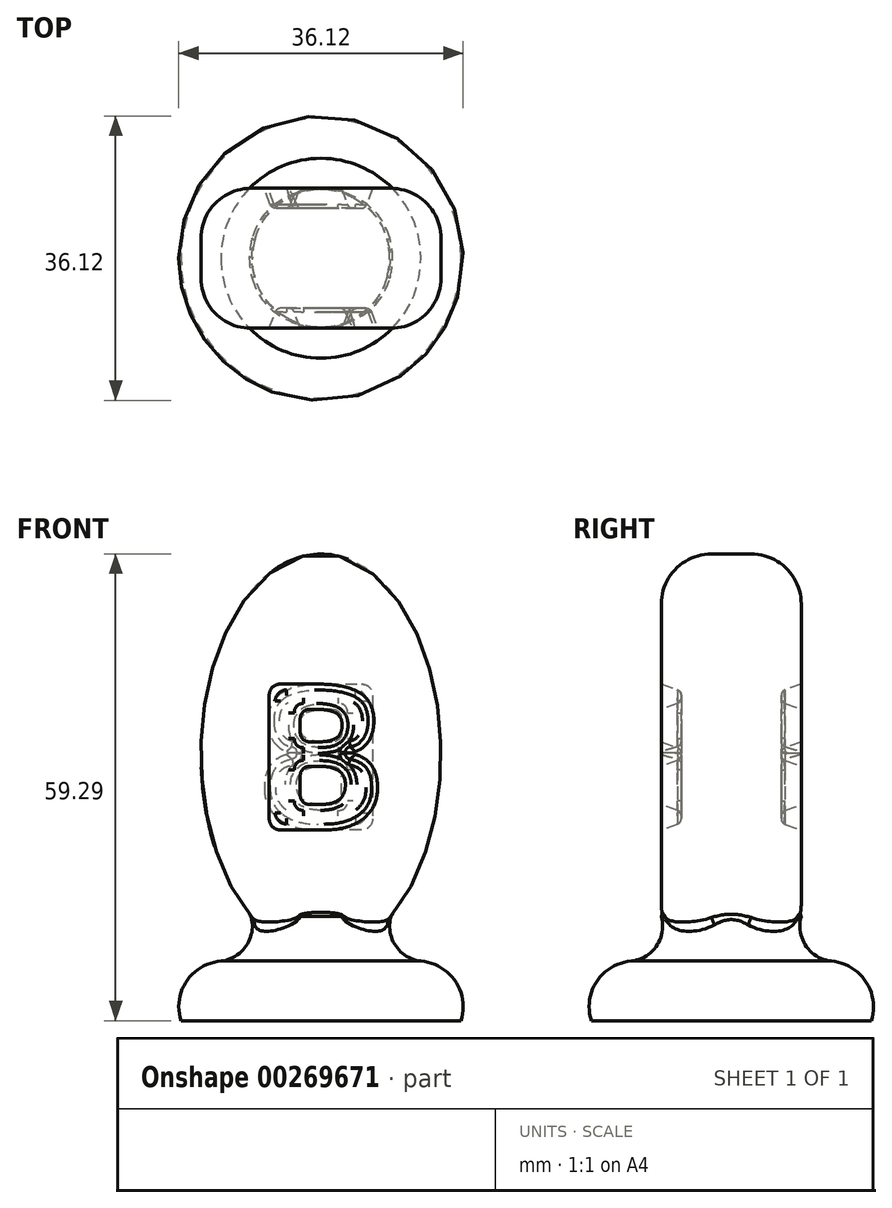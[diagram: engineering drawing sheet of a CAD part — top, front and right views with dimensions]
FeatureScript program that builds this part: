
annotation { "Feature Type Name" : "Feature", "Feature Type Description" : "" }
export const myFeature = defineFeature(function(context is Context, id is Id, definition is map)
    precondition{}
    {
        {
            var Q0;
            Q0=qCreatedBy(makeId("Front.planeOp"),FACE);
            var sketch = newSketch(context, id + "F0", { "sketchPlane" : qUnion([Q0])});
            skEllipse(sketch, "E0", {"center": v(0, 33.89) * mm, "majorRadius": 25.4 * mm, "minorRadius": 15.24 * mm, "majorAxis": v(0, -1)});
            skLineSegment(sketch, "E1", {"start": v(0, 0) * mm, "end": v(0, 8.49) * mm, "construction": true});
            skSolve(sketch);
        }
        {
            var Q0;
            Q0=qSketchRegion(id+"F0",true);
            extrude(context, id + "F1", {"entities" : qUnion([Q0]), "depth" : 8.9 * mm});
        }
        {
            var Q0;
            Q0=makeQuery(id+"F1.opExtrude","CAP_EDGE",EDGE,{"disambiguationData":[OSD([sQuery(id+"F0.wireOp",EDGE,"E0")])],"isStart":false});
            fillet(context, id + "F2", {"entities" : qUnion([Q0]), "radius" : 6.35 * mm, "tangentPropagation" : true, "allowEdgeOverflow" : false});
        }
        {
            var Q0;
            Q0=qCreatedBy(makeId("Front.planeOp"),FACE);
            var sketch = newSketch(context, id + "F3", { "sketchPlane" : qUnion([Q0])});
            skLineSegment(sketch, "E2", {"start": v(0, 0) * mm, "end": v(-17.78, 0) * mm});
            skLineSegment(sketch, "E3", {"start": v(-17.78, 0) * mm, "end": v(0, 26.51) * mm});
            skLineSegment(sketch, "E4", {"start": v(0, 26.51) * mm, "end": v(0, 0) * mm});
            skArc(sketch, "E5", {"start": v(-12.7, 7.57) * mm, "mid": v(-17.07, 5.02) * mm, "end": v(-17.78, 0) * mm});
            skArc(sketch, "E6", {"start": v(-12.7, 7.57) * mm, "mid": v(-9.48, 9.53) * mm, "end": v(-8.9, 13.26) * mm});
            skLineSegment(sketch, "E7", {"start": v(0, 0) * mm, "end": v(0, -19.3) * mm, "construction": true});
            skSolve(sketch);
        }
        {
            var Q0;
            {var subQ0=sQuery(id+"F3.wireOp",EDGE,"E5");Q0=makeQuery(id+"F3.imprint","IMPRINT",FACE,{"disambiguationData":[TD([[makeQuery(id+"F3.imprint","IMPRINT",EDGE,{"derivedFrom":subQ0}),1.0]])]});}
            var Q1;
            {var subQ4=sQuery(id+"F3.wireOp",EDGE,"E2");Q1=makeQuery(id+"F3.imprint","IMPRINT",FACE,{"disambiguationData":[TD([[makeQuery(id+"F3.imprint","IMPRINT",EDGE,{"derivedFrom":subQ4}),-1.0]])]});}
            var Q2;
            Q2=sQuery(id+"F3.wireOp",EDGE,"E7");
            revolve(context, id + "F4", {"entities" : qUnion([Q0, Q1]), "axis" : qUnion([Q2]), "revolveType" : RevolveType.ONE_DIRECTION, "oppositeDirection" : true, "angle" : 180 * degree});
        }
        {
            var Q0;
            Q0=makeQuery(id+"F1.opExtrude","CAP_FACE",FACE,{"disambiguationData":[OSD([sQuery(id+"F0.wireOp",EDGE,"E0")])],"isStart":false});
            var sketch = newSketch(context, id + "F5", { "sketchPlane" : qUnion([Q0])});
            skSolve(sketch);
        }
        {
            var Q0;
            {var subQ0=sQuery(id+"F0.wireOp",EDGE,"E0");Q0=makeQuery(id+"F5.imprint","IMPRINT",FACE,{"disambiguationData":[TD([[makeQuery(id+"F5.imprint","IMPRINT",EDGE,{"derivedFrom":makeQuery(id+"F2.opFillet","BLEND_EDGE",EDGE,{"blendedFrom":[makeQuery(id+"F1.opExtrude","CAP_EDGE",EDGE,{"disambiguationData":[OSD([subQ0])],"isStart":false}),makeQuery(id+"F1.opExtrude","CAP_FACE",FACE,{"disambiguationData":[OSD([subQ0])],"isStart":false})],"blendedInto":[makeQuery(id+"F1.opExtrude","CAP_FACE",FACE,{"disambiguationData":[OSD([subQ0])],"isStart":false})]})}),1.0]])]});}
            var sketch = newSketch(context, id + "F6", { "sketchPlane" : qUnion([Q0])});
            skText(sketch, "E8", { "text": "B", "fontName": "OpenSans-Bold.ttf"});
            const initialGuessF6  = {"E8": [-0.0089, 0.02422, 1, 0, 0.01871]};
            skSetInitialGuess(sketch, initialGuessF6);
            skSolve(sketch);
        }
        {
            var Q0;
            Q0=qSketchRegion(id+"F6",true);
            extrude(context, id + "F7", {"entities" : qUnion([Q0]), "operationType" : NewBodyOperationType.REMOVE, "oppositeDirection" : true, "depth" : 2.54 * mm, "hasDraft" : true, "draftAngle" : 20 * degree, "draftPullDirection" : true});
        }
        {
            var Q0;
            Q0=makeQuery(id+"F7.boolean.opBoolean","COPY",EDGE,{"derivedFrom":makeQuery(id+"F7.opExtrude","SWEPT_EDGE",EDGE,{"disambiguationData":[OSD([sQuery(id+"F6.wireOp",EDGE,"E8.sketch_text.stroke-10"),sQuery(id+"F6.wireOp",EDGE,"E8.sketch_text.stroke-11")])]})});
            var Q1;
            Q1=makeQuery(id+"F7.boolean.opBoolean","COPY",EDGE,{"derivedFrom":makeQuery(id+"F7.opExtrude","SWEPT_EDGE",EDGE,{"disambiguationData":[OSD([sQuery(id+"F6.wireOp",EDGE,"E8.sketch_text.stroke-0"),sQuery(id+"F6.wireOp",EDGE,"E8.sketch_text.stroke-11")])]})});
            fillet(context, id + "F8", {"entities" : qUnion([Q0, Q1]), "radius" : 1.52 * mm, "tangentPropagation" : true, "allowEdgeOverflow" : false});
        }
        {
            var Q0;
            Q0=makeQuery(id+"F7.boolean.opBoolean","COPY",EDGE,{"derivedFrom":makeQuery(id+"F7.opExtrude","SWEPT_EDGE",EDGE,{"disambiguationData":[OSD([sQuery(id+"F6.wireOp",EDGE,"E8.sketch_text.stroke-15"),sQuery(id+"F6.wireOp",EDGE,"E8.sketch_text.stroke-16")])]})});
            var Q1;
            Q1=makeQuery(id+"F7.boolean.opBoolean","COPY",EDGE,{"derivedFrom":makeQuery(id+"F7.opExtrude","SWEPT_EDGE",EDGE,{"disambiguationData":[OSD([sQuery(id+"F6.wireOp",EDGE,"E8.sketch_text.stroke-14"),sQuery(id+"F6.wireOp",EDGE,"E8.sketch_text.stroke-15")])]})});
            var Q2;
            Q2=makeQuery(id+"F7.boolean.opBoolean","COPY",EDGE,{"derivedFrom":makeQuery(id+"F7.opExtrude","SWEPT_EDGE",EDGE,{"disambiguationData":[OSD([sQuery(id+"F6.wireOp",EDGE,"E8.sketch_text.stroke-8"),sQuery(id+"F6.wireOp",EDGE,"E8.sketch_text.stroke-9")])]})});
            var Q3;
            Q3=makeQuery(id+"F7.boolean.opBoolean","COPY",EDGE,{"derivedFrom":makeQuery(id+"F7.opExtrude","SWEPT_EDGE",EDGE,{"disambiguationData":[OSD([sQuery(id+"F6.wireOp",EDGE,"E8.sketch_text.stroke-7"),sQuery(id+"F6.wireOp",EDGE,"E8.sketch_text.stroke-8")])]})});
            var Q4;
            Q4=makeQuery(id+"F7.boolean.opBoolean","COPY",EDGE,{"derivedFrom":makeQuery(id+"F7.opExtrude","SWEPT_EDGE",EDGE,{"disambiguationData":[OSD([sQuery(id+"F6.wireOp",EDGE,"E8.sketch_text.stroke-7"),sQuery(id+"F6.wireOp",EDGE,"E8.sketch_text.stroke-18")])]})});
            var Q5;
            Q5=makeQuery(id+"F7.boolean.opBoolean","COPY",EDGE,{"derivedFrom":makeQuery(id+"F7.opExtrude","SWEPT_EDGE",EDGE,{"disambiguationData":[OSD([sQuery(id+"F6.wireOp",EDGE,"E8.sketch_text.stroke-17"),sQuery(id+"F6.wireOp",EDGE,"E8.sketch_text.stroke-18")])]})});
            var Q6;
            Q6=makeQuery(id+"F7.boolean.opBoolean","COPY",EDGE,{"derivedFrom":makeQuery(id+"F7.opExtrude","SWEPT_EDGE",EDGE,{"disambiguationData":[OSD([sQuery(id+"F6.wireOp",EDGE,"E8.sketch_text.stroke-19"),sQuery(id+"F6.wireOp",EDGE,"E8.sketch_text.stroke-20")])]})});
            var Q7;
            Q7=makeQuery(id+"F7.boolean.opBoolean","COPY",EDGE,{"derivedFrom":makeQuery(id+"F7.opExtrude","SWEPT_EDGE",EDGE,{"disambiguationData":[OSD([sQuery(id+"F6.wireOp",EDGE,"E8.sketch_text.stroke-19"),sQuery(id+"F6.wireOp",EDGE,"E8.sketch_text.stroke-24")])]})});
            fillet(context, id + "F9", {"entities" : qUnion([Q0, Q1, Q2, Q3, Q4, Q5, Q6, Q7]), "radius" : 1.27 * mm, "tangentPropagation" : true, "allowEdgeOverflow" : false});
        }
        {
            var Q0;
            Q0=makeQuery(id+"F7.boolean.opBoolean","COPY",EDGE,{"derivedFrom":makeQuery(id+"F7.opExtrude","SWEPT_EDGE",EDGE,{"disambiguationData":[OSD([sQuery(id+"F6.wireOp",EDGE,"E8.sketch_text.stroke-16"),sQuery(id+"F6.wireOp",EDGE,"E8.sketch_text.stroke-17")])]})});
            var Q1;
            Q1=makeQuery(id+"F7.boolean.opBoolean","COPY",EDGE,{"derivedFrom":makeQuery(id+"F7.opExtrude","SWEPT_EDGE",EDGE,{"disambiguationData":[OSD([sQuery(id+"F6.wireOp",EDGE,"E8.sketch_text.stroke-5"),sQuery(id+"F6.wireOp",EDGE,"E8.sketch_text.stroke-6")])]})});
            var Q2;
            Q2=makeQuery(id+"F7.boolean.opBoolean","COPY",EDGE,{"derivedFrom":makeQuery(id+"F7.opExtrude","SWEPT_EDGE",EDGE,{"disambiguationData":[OSD([sQuery(id+"F6.wireOp",EDGE,"E8.sketch_text.stroke-0"),sQuery(id+"F6.wireOp",EDGE,"E8.sketch_text.stroke-6")])]})});
            var Q3;
            Q3=makeQuery(id+"F7.boolean.opBoolean","COPY",EDGE,{"derivedFrom":makeQuery(id+"F7.opExtrude","SWEPT_EDGE",EDGE,{"disambiguationData":[OSD([sQuery(id+"F6.wireOp",EDGE,"E8.sketch_text.stroke-4"),sQuery(id+"F6.wireOp",EDGE,"E8.sketch_text.stroke-5")])]})});
            fillet(context, id + "F10", {"entities" : qUnion([Q0, Q1, Q2, Q3]), "radius" : 0.76 * mm, "tangentPropagation" : true, "allowEdgeOverflow" : false});
        }
        {
            var Q0;
            Q0=makeQuery(id+"F7.boolean.opBoolean","COPY",EDGE,{"derivedFrom":makeQuery(id+"F7.opExtrude","CAP_EDGE",EDGE,{"disambiguationData":[OSD([sQuery(id+"F6.wireOp",EDGE,"E8.sketch_text.stroke-6")])],"isStart":false})});
            var Q1;
            Q1=makeQuery(id+"F7.boolean.opBoolean","COPY",EDGE,{"derivedFrom":makeQuery(id+"F7.opExtrude","CAP_EDGE",EDGE,{"disambiguationData":[OSD([sQuery(id+"F6.wireOp",EDGE,"E8.sketch_text.stroke-7")])],"isStart":false})});
            var Q2;
            Q2=makeQuery(id+"F7.boolean.opBoolean","COPY",EDGE,{"derivedFrom":makeQuery(id+"F7.opExtrude","CAP_EDGE",EDGE,{"disambiguationData":[OSD([sQuery(id+"F6.wireOp",EDGE,"E8.sketch_text.stroke-18")])],"isStart":false})});
            var Q3;
            Q3=makeQuery(id+"F7.boolean.opBoolean","COPY",EDGE,{"derivedFrom":makeQuery(id+"F7.opExtrude","CAP_EDGE",EDGE,{"disambiguationData":[OSD([sQuery(id+"F6.wireOp",EDGE,"E8.sketch_text.stroke-19")])],"isStart":false})});
            fillet(context, id + "F11", {"entities" : qUnion([Q0, Q1, Q2, Q3]), "radius" : 0.76 * mm, "tangentPropagation" : true, "allowEdgeOverflow" : false});
        }
        {
            var Q0;
            Q0=makeQuery(id+"F4.opRevolve","SWEPT_BODY",BODY,{"disambiguationData":[OSD([sQuery(id+"F3.wireOp",EDGE,"E2"),sQuery(id+"F3.wireOp",EDGE,"E3"),sQuery(id+"F3.wireOp",EDGE,"E4"),sQuery(id+"F3.wireOp",EDGE,"E5"),sQuery(id+"F3.wireOp",EDGE,"E6")])]});
            var Q1;
            Q1=makeQuery(id+"F1.opExtrude","SWEPT_BODY",BODY,{"disambiguationData":[OSD([sQuery(id+"F0.wireOp",EDGE,"E0")])]});
            booleanBodies(context, id + "F12", {"operationType" : BooleanOperationType.UNION, "tools" : qUnion([Q0, Q1])});
        }
        {
            var Q0;
            Q0=makeQuery(id+"F4.opRevolve","SWEPT_BODY",BODY,{"disambiguationData":[OSD([sQuery(id+"F3.wireOp",EDGE,"E2"),sQuery(id+"F3.wireOp",EDGE,"E3"),sQuery(id+"F3.wireOp",EDGE,"E4"),sQuery(id+"F3.wireOp",EDGE,"E5"),sQuery(id+"F3.wireOp",EDGE,"E6")])]});
            var Q1;
            Q1=sQuery(id+"F3.wireOp",EDGE,"E7");
            circularPattern(context, id + "F13", {"operationType" : NewBodyOperationType.ADD, "entities" : qUnion([Q0]), "axis" : qUnion([Q1]), "angle" : 360 * degree, "instanceCount" : 2, "equalSpace" : true});
        }
        {
            var Q0;
            Q0=makeQuery(id+"F12.opBoolean","INTERSECT",EDGE,{"disambiguationData":[OD(1.0)],"derivedFrom":[makeQuery(id+"F2.opFillet","BLEND_FACE",FACE,{"disambiguationData":[OSD([sQuery(id+"F0.wireOp",EDGE,"E0")])]}),makeQuery(id+"F4.opRevolve","SWEPT_FACE",FACE,{"disambiguationData":[OSD([sQuery(id+"F3.wireOp",EDGE,"E6")])]})]});
            var Q1;
            Q1=makeQuery(id+"F12.opBoolean","INTERSECT",EDGE,{"disambiguationData":[OD(0.0)],"derivedFrom":[makeQuery(id+"F2.opFillet","BLEND_FACE",FACE,{"disambiguationData":[OSD([sQuery(id+"F0.wireOp",EDGE,"E0")])]}),makeQuery(id+"F4.opRevolve","SWEPT_FACE",FACE,{"disambiguationData":[OSD([sQuery(id+"F3.wireOp",EDGE,"E6")])]})]});
            fillet(context, id + "F14", {"entities" : qUnion([Q0, Q1]), "radius" : 1.52 * mm, "tangentPropagation" : true, "allowEdgeOverflow" : false});
        }
        {
            var Q0;
            Q0=makeQuery(id+"F12.opBoolean","INTERSECT",EDGE,{"derivedFrom":[makeQuery(id+"F2.opFillet","BLEND_FACE",FACE,{"disambiguationData":[OSD([sQuery(id+"F0.wireOp",EDGE,"E0")])]}),makeQuery(id+"F4.opRevolve","SWEPT_FACE",FACE,{"disambiguationData":[OSD([sQuery(id+"F3.wireOp",EDGE,"E3")])]})]});
            var Q1;
            Q1=makeQuery(id+"F13.opPattern","COPY",EDGE,{"derivedFrom":makeQuery(id+"F12.opBoolean","INTERSECT",EDGE,{"derivedFrom":[makeQuery(id+"F2.opFillet","BLEND_FACE",FACE,{"disambiguationData":[OSD([sQuery(id+"F0.wireOp",EDGE,"E0")])]}),makeQuery(id+"F4.opRevolve","SWEPT_FACE",FACE,{"disambiguationData":[OSD([sQuery(id+"F3.wireOp",EDGE,"E3")])]})]}),"instanceName":"1"});
            fillet(context, id + "F15", {"entities" : qUnion([Q0, Q1]), "radius" : 0.76 * mm, "tangentPropagation" : true, "allowEdgeOverflow" : false});
        }
    });
